# Revit family: VLN_Aqua_B9318_BIM_NL
name_source: partatom
category: Plumbing Fixtures
revit_build: Autodesk Revit MEP 2014 (Build: 20130308_1515(x64)
units: mm (PartAtom-declared; Revit-internal decimal feet)

## types (1)
- B9318AA - AQUA L3 SHK 3F/100 600MM MET/1750 SD VLN
    Accessories = www.idealstandardnederland.nl
    AreaUnits = millimeters
    Assembly Code = C1030200
    AssetType = Vast
    BIMObjectName = VLN_Venlo_ShowerFittingsPackage_B9318AA
    BREEAMApproved = No
    BarCode = 3800861023562
    Brand = Venlo
    CWFU = 0
    Color = Chroom
    ConnectionType = Sanitair
    Cost = 0 $
    Default Elevation = 800 mm  [stored 2.62467 ft]
    Description = Venlo Aqua 100 glijstangcombinatie 600 mm. Handdouche 3 functies (Normaal / Champage / Massage). Glijstang 600 mm met renovatiefunctie. Zeepschaal & doucheslang "Metalflex" 1750 mm. 8 l/min bij 3 bar.
    DurationUnit = jaar
    ECA = No
    ExpectedLife = 25
    Features = Glijstangcombinatie 600 mm. Handdouche 3 functies (Normaal / Champage / Massage). Glijstang 600 mm met renovatiefunctie. Zeepschaal & doucheslang "Metalflex" 1750 mm. 8 l/min bij 3 bar.
    Finish = Chroom
    HWFU = 0
    IfcExportAs = IfcValveType
    IfcExportType = FAUCET
    InstallationInstructions = http://www.idealstandardnederland.nl
    LinearUnits = millimeters
    ManufacturerURL = www.idealstandardnederland.nl
    Material = Messing
    Model = B9318AA
    ModelNumber = B9318AA
    ModelReference = Venlo Aqua 100 glijstangcombinatie 600 mm. Handdouche 3 functies (Normaal / Champage / Massage). Glijstang 600 mm met renovatiefunctie. Zeepschaal & doucheslang "Metalflex" 1750 mm. 8 l/min bij 3 bar.
    NBSDescription = Shower fittings package
    NBSReference = 45-35-70/330
    Name = ShowerFittingsPackage_B9318AA_Venlo
    NettWeight = 1.165 kg
    NominalHeight = 603 mm
    NominalLength = 182 mm
    NominalWidth = 149 mm
    ProductInformation = http://www.idealstandardnederland.nl
    Shape = Gesculptuurd
    Size = 149 x 182 x 603 mm
    Space = Internal
    SpareParts = www.idealstandardnederland.nl
    TMV3 = No
    TestPressure = 10 Bar
    URL = www.idealstandardnederland.nl
    Uniclass2015Code = Pr_40_20_87_75
    Uniclass2015Title = Shower fittings package
    Uniclass2015Version = Products v1.1
    Version = 1
    VolumeUnits = liter
    WFU = 0
    WRAS = No
    WarrantyDescription = Fabrieksgarantie
    WarrantyDurationParts = 5
    WarrantyDurationUnit = jaar
    WaterEfficientProduct = No
    WorkingPressure = 1-5 bar

note: [stored X ft] marks values corroborated as IEEE doubles in the binary element streams (Revit-internal decimal feet)

## geometry (parser evidence)
native form markers: Sweep x1
no freeform markers — native parametric forms only
